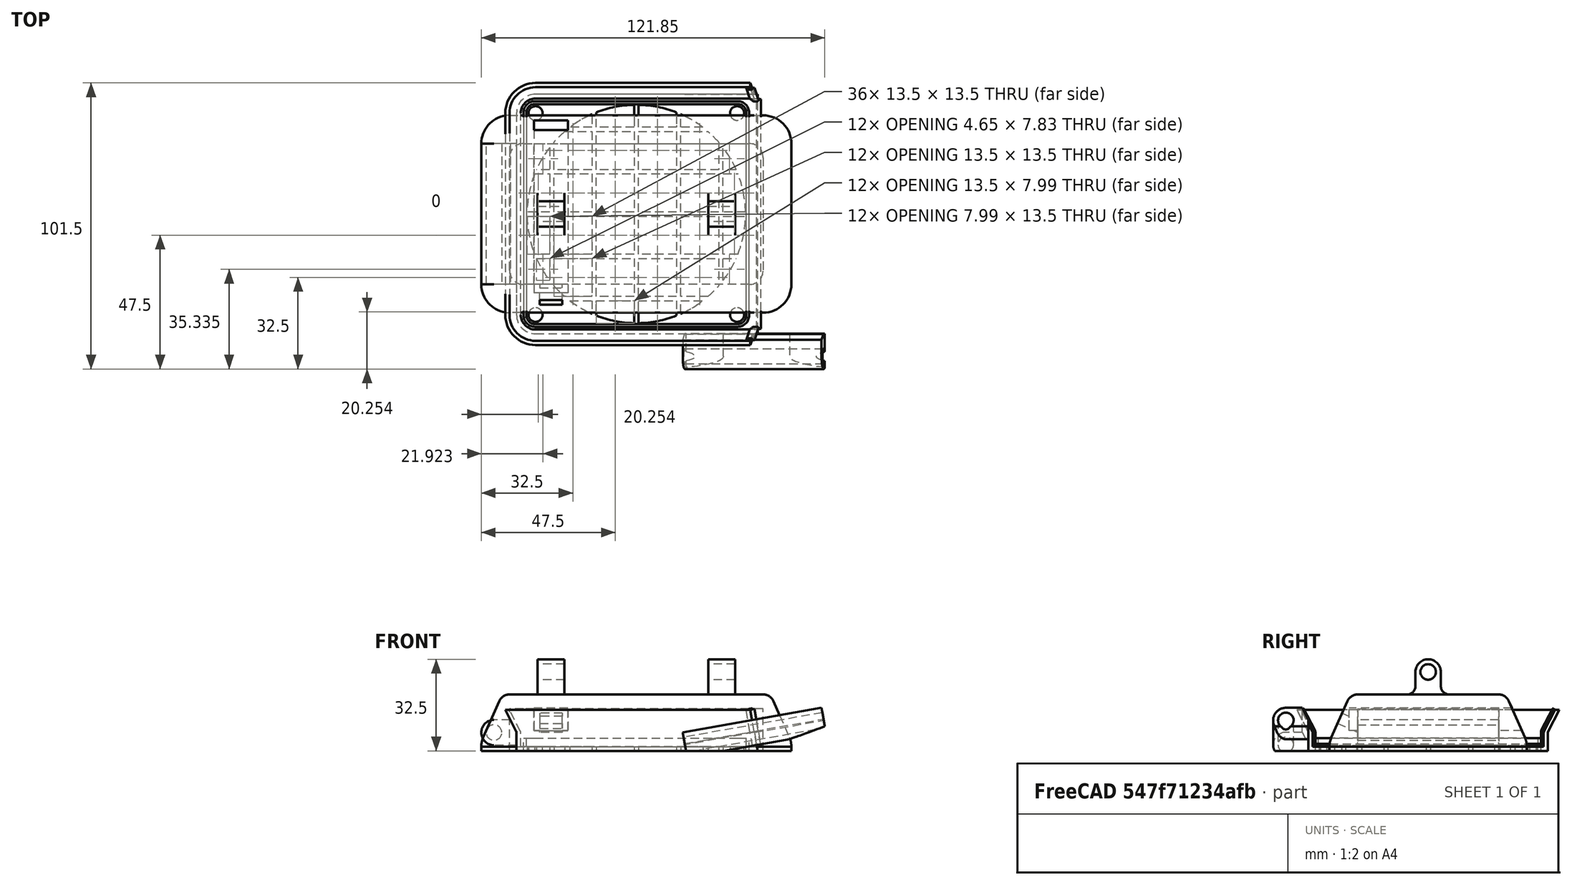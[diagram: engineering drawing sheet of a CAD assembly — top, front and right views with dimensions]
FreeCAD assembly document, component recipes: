
FREECAD ASSEMBLY — COMPONENT RECIPES ("Solder Fume Extractor 2x80mm fans")

This assembly document has 5 components, labeled P0..P4 below (a component is one placed body or linked part). 5 of them carry a construction recipe — the FreeCAD feature program that regenerates the part from scratch, quoted from this document or its linked companion documents; the rest are supplied as boundary geometry only. No exploded tour is included for this assembly.
COMPONENT P0 — recipe-attached ("Fan1Holder", modeled in this document).
Construction recipe (the document's own serialized feature program — sketch geometry with constraints, then the solid features built on it; lengths are millimeters unless a unit is written):

FEATURE [Sketcher::SketchObject] Sketch
  ArcFitTolerance = 1e-06
  AttachmentSupport = -> [XY_Plane]
  FullyConstrained = true
  MakeInternals = false
  MapMode = 5
  sketch-geometry (13):
    g0: LineSegment StartX=-42.5 StartY=35.75 StartZ=0 EndX=-42.5 EndY=-35.75 EndZ=0
    g1: LineSegment StartX=-35.75 StartY=-42.5 StartZ=0 EndX=60 EndY=-42.5 EndZ=0
    g2: LineSegment StartX=60 StartY=-42.5 StartZ=0 EndX=60 EndY=42.5 EndZ=0
    g3: LineSegment StartX=60 StartY=42.5 StartZ=0 EndX=-35.75 EndY=42.5 EndZ=0
    g4: Circle CenterX=-35.75 CenterY=35.75 CenterZ=0 NormalX=0 NormalY=0 NormalZ=1 AngleXU=0 Radius=2.5
    g5: Circle CenterX=35.75 CenterY=35.75 CenterZ=0 NormalX=0 NormalY=0 NormalZ=1 AngleXU=0 Radius=2.5
    g6: Circle CenterX=-35.75 CenterY=-35.75 CenterZ=0 NormalX=0 NormalY=0 NormalZ=1 AngleXU=0 Radius=2.5
    g7: Circle CenterX=35.75 CenterY=-35.75 CenterZ=0 NormalX=0 NormalY=0 NormalZ=1 AngleXU=0 Radius=2.5
    g8: Circle CenterX=0 CenterY=0 CenterZ=0 NormalX=0 NormalY=0 NormalZ=1 AngleXU=0 Radius=38.75
    g9: ArcOfCircle CenterX=-35.75 CenterY=35.75 CenterZ=0 NormalX=0 NormalY=0 NormalZ=1 AngleXU=0 Radius=6.75 StartAngle=1.5708 EndAngle=3.14159
    g10: GeomPoint [constr] X=-42.5 Y=42.5 Z=0
    g11: ArcOfCircle CenterX=-35.75 CenterY=-35.75 CenterZ=0 NormalX=0 NormalY=0 NormalZ=1 AngleXU=0 Radius=6.75 StartAngle=3.14159 EndAngle=4.71239
    g12: GeomPoint [constr] X=-42.5 Y=-42.5 Z=0
  constraints (30):
    c: Coincident(g1,g2)
    c: Coincident(g2,g3)
    c: Vertical(g2)
    c: Horizontal(g1)
    c: Horizontal(g3)
    c: DistanceY(g12,g10) = 85
    c: Equal(g7,g5)
    c: Equal(g5,g4)
    c: Equal(g4,g6)
    c: Diameter(g7) = 5
    c: Symmetric(g7,g5,g-1)
    c: Symmetric(g5,g4,g-2)
    c: Vertical(g6,g4)
    c: Horizontal(g6,g7)
    c: DistanceX(g4,g5) = 71.5
    c: DistanceY(g6,g4) = 71.5
    c: Symmetric(g12,g10,g-1)
    c: Coincident(g8,g-1)
    c: Diameter(g8) = 77.5
    c: DistanceX(g10,g-1) = 42.5
    c: DistanceX(g1) = 60
    c: PointOnObject(g10,g0)
    c: PointOnObject(g10,g3)
    c: Tangent(g0,g9) = -1.5708
    c: Tangent(g3,g9) = -1.5708
    c: PointOnObject(g12,g1)
    c: Tangent(g0,g11) = -1.5708
    c: Tangent(g1,g11) = -1.5708
    c: Equal(g11,g9)
    c: Coincident(g9,g4)
FEATURE [PartDesign::Pad] Pad
  Direction = (0,0,1)
  Length = 1.5
  Length2 = 10
  Profile = -> Sketch
  ReferenceAxis = -> Sketch [N_Axis]
  Refine = true
  Suppressed = false
  Type = 0
FEATURE [Sketcher::SketchObject] Sketch001
  ArcFitTolerance = 1e-06
  AttachmentSupport = -> [Pad]
  ExternalGeometry = -> [Pad]
  FullyConstrained = true
  MakeInternals = false
  MapMode = 5
  Placement = pos=(0,0,1.5) rot=(0,0,1;0rad)
  sketch-geometry (12):
    g0: LineSegment StartX=60 StartY=42.5 StartZ=0 EndX=-35.75 EndY=42.5 EndZ=0
    g1: LineSegment StartX=-42.5 StartY=35.75 StartZ=0 EndX=-42.5 EndY=-35.75 EndZ=0
    g2: LineSegment StartX=-35.75 StartY=-42.5 StartZ=0 EndX=60 EndY=-42.5 EndZ=0
    g3: ArcOfCircle CenterX=-35.75 CenterY=-35.75 CenterZ=0 NormalX=0 NormalY=0 NormalZ=1 AngleXU=0 Radius=6.75 StartAngle=3.14159 EndAngle=4.71239
    g4: ArcOfCircle CenterX=-35.75 CenterY=35.75 CenterZ=0 NormalX=0 NormalY=0 NormalZ=1 AngleXU=0 Radius=6.75 StartAngle=1.5708 EndAngle=3.14159
    g5: LineSegment StartX=60 StartY=-42.5 StartZ=0 EndX=60 EndY=-41 EndZ=0
    g6: LineSegment StartX=60 StartY=-41 StartZ=0 EndX=-35.75 EndY=-41 EndZ=0
    g7: LineSegment StartX=-41 StartY=-35.75 StartZ=0 EndX=-41 EndY=35.75 EndZ=0
    g8: LineSegment StartX=-35.75 StartY=41 StartZ=0 EndX=60 EndY=41 EndZ=0
    g9: LineSegment StartX=60 StartY=41 StartZ=0 EndX=60 EndY=42.5 EndZ=0
    g10: ArcOfCircle CenterX=-35.75 CenterY=-35.75 CenterZ=0 NormalX=0 NormalY=0 NormalZ=1 AngleXU=0 Radius=5.25 StartAngle=3.14159 EndAngle=4.71239
    g11: ArcOfCircle CenterX=-35.75 CenterY=35.75 CenterZ=0 NormalX=0 NormalY=0 NormalZ=1 AngleXU=0 Radius=5.25 StartAngle=1.5708 EndAngle=3.14159
  constraints (30):
    c: Coincident(g0,g-3)
    c: Coincident(g0,g-4)
    c: Horizontal(g2)
    c: Symmetric(g2,g0,g-1)
    c: Equal(g2,g0)
    c: Coincident(g-5,g1)
    c: Coincident(g1,g-5)
    c: Coincident(g3,g2)
    c: Coincident(g3,g1)
    c: Coincident(g4,g1)
    c: Coincident(g4,g0)
    c: Equal(g4,g-4)
    c: Equal(g-4,g3)
    c: Coincident(g5,g2)
    c: Vertical(g5)
    c: Coincident(g6,g5)
    c: Horizontal(g6)
    c: Vertical(g7)
    c: Coincident(g9,g8)
    c: Coincident(g9,g0)
    c: Horizontal(g8)
    c: Vertical(g9)
    c: Equal(g5,g9)
    c: Equal(g6,g8)
    c: Tangent(g10,g6) = 1.5708
    c: Tangent(g10,g7) = 1.5708
    c: Tangent(g11,g7) = 1.5708
    c: Tangent(g11,g8) = 1.5708
    c: DistanceY(g5,g5) = 1.5
    c: Coincident(g11,g4)
FEATURE [PartDesign::Pad] Pad001
  BaseFeature = -> Pad
  Direction = (0,0,1)
  Length = 5
  Length2 = 10
  Profile = -> Sketch001
  ReferenceAxis = -> Sketch001 [N_Axis]
  Refine = true
  Suppressed = false
  Type = 0
FEATURE [Sketcher::SketchObject] Sketch002
  ArcFitTolerance = 1e-06
  AttachmentSupport = -> [Pad001]
  ExternalGeometry = -> [Pad001]
  FullyConstrained = true
  MakeInternals = false
  MapMode = 5
  Placement = pos=(60,0,0) rot=(0.57735,0.57735,0.57735;2.0944rad)
  sketch-geometry (6):
    g0: LineSegment StartX=41.1112 StartY=6.9583 StartZ=0 EndX=45 EndY=14.5 EndZ=0
    g1: LineSegment StartX=45 StartY=14.5 StartZ=0 EndX=46.5 EndY=14.5 EndZ=0
    g2: LineSegment StartX=46.5 StartY=14.5 StartZ=0 EndX=42.6112 EndY=6.9583 EndZ=0
    g3: ArcOfCircle CenterX=43.5 CenterY=6.5 CenterZ=0 NormalX=0 NormalY=0 NormalZ=1 AngleXU=0 Radius=1 StartAngle=2.66551 EndAngle=3.14159
    g4: ArcOfCircle CenterX=42 CenterY=6.5 CenterZ=0 NormalX=0 NormalY=0 NormalZ=1 AngleXU=0 Radius=1 StartAngle=2.66551 EndAngle=3.14159
    g5: LineSegment StartX=42.5 StartY=6.5 StartZ=0 EndX=41 EndY=6.5 EndZ=0
  constraints (16):
    c: Coincident(g0,g1)
    c: Horizontal(g1)
    c: Coincident(g1,g2)
    c: Coincident(g3,g-3)
    c: Coincident(g4,g-3)
    c: Tangent(g4,g0) = 1.5708
    c: Tangent(g3,g2) = -1.5708
    c: Coincident(g5,g3)
    c: Coincident(g5,g4)
    c: Perpendicular(g3,g5)
    c: Perpendicular(g4,g5)
    c: Equal(g1,g5)
    c: Radius(g4) = 1
    c: DistanceY(g3,g1) = 8
    c: DistanceX(g3,g1) = 4
    c: Equal(g4,g3)
FEATURE [PartDesign::AdditivePipe] AdditivePipe
  AuxilleryCurvelinear = true
  AuxillerySpineTangent = false
  BaseFeature = -> Pad001
  Binormal = (0,0,0)
  Mode = 0
  Profile = -> Sketch002
  Refine = true
  Spine = -> Pad001 [Edge32,Edge33,Edge34,Edge35,Edge36]
  SpineTangent = false
  Suppressed = false
  Transformation = 0
  Transition = 0
FEATURE [Sketcher::SketchObject] Sketch003
  ArcFitTolerance = 1e-06
  AttachmentSupport = -> [XY_Plane]
  ExternalGeometry = -> [AdditivePipe]
  FullyConstrained = true
  MakeInternals = false
  MapMode = 5
  sketch-geometry (5):
    g0: LineSegment StartX=-30.75 StartY=42.5 StartZ=0 EndX=-30.75 EndY=-42.5 EndZ=0
    g1: LineSegment StartX=-30.75 StartY=-42.5 StartZ=0 EndX=-29.25 EndY=-42.5 EndZ=0
    g2: LineSegment StartX=-29.25 StartY=-42.5 StartZ=0 EndX=-29.25 EndY=42.5 EndZ=0
    g3: LineSegment StartX=-29.25 StartY=42.5 StartZ=0 EndX=-30.75 EndY=42.5 EndZ=0
    g4: GeomPoint [constr] X=-30 Y=0 Z=0
  constraints (13):
    c: Coincident(g0,g1)
    c: Coincident(g1,g2)
    c: Coincident(g2,g3)
    c: Coincident(g3,g0)
    c: Vertical(g0)
    c: Vertical(g2)
    c: Horizontal(g1)
    c: Horizontal(g3)
    c: Symmetric(g2,g0,g4)
    c: PointOnObject(g4,g-1)
    c: PointOnObject(g1,g-3)
    c: DistanceX(g3,g3) = 1.5
    c: DistanceX(g4,g-1) = 30
FEATURE [PartDesign::Pad] Pad002
  BaseFeature = -> AdditivePipe
  Direction = (0,0,1)
  Length = 10
  Length2 = 10
  Profile = -> Sketch003
  ReferenceAxis = -> Sketch003 [N_Axis]
  Refine = true
  Suppressed = false
  Type = 3
  UpToFace = -> AdditivePipe [Face2]
FEATURE [PartDesign::LinearPattern] LinearPattern
  BaseFeature = -> Pad002
  Direction = -> Sketch003 [H_Axis]
  Length = 60
  Mode = 0
  Occurrences = 5
  Offset = 15
  Originals = -> [Pad002]
  Refine = true
  Suppressed = false
  TransformMode = 0
FEATURE [Sketcher::SketchObject] Sketch004
  ArcFitTolerance = 1e-06
  AttachmentSupport = -> [XY_Plane]
  ExternalGeometry = -> [LinearPattern]
  FullyConstrained = true
  MakeInternals = false
  MapMode = 5
  sketch-geometry (5):
    g0: LineSegment StartX=42.5 StartY=29.25 StartZ=0 EndX=42.5 EndY=30.75 EndZ=0
    g1: LineSegment StartX=42.5 StartY=30.75 StartZ=0 EndX=-42.5 EndY=30.75 EndZ=0
    g2: LineSegment StartX=-42.5 StartY=30.75 StartZ=0 EndX=-42.5 EndY=29.25 EndZ=0
    g3: LineSegment StartX=-42.5 StartY=29.25 StartZ=0 EndX=42.5 EndY=29.25 EndZ=0
    g4: GeomPoint [constr] X=0 Y=30 Z=0
  constraints (13):
    c: Coincident(g0,g1)
    c: Coincident(g1,g2)
    c: Coincident(g2,g3)
    c: Coincident(g3,g0)
    c: Vertical(g0)
    c: Vertical(g2)
    c: Horizontal(g1)
    c: Horizontal(g3)
    c: Symmetric(g2,g0,g4)
    c: PointOnObject(g4,g-2)
    c: PointOnObject(g1,g-3)
    c: DistanceY(g4) = 30
    c: DistanceY(g0,g0) = 1.5
FEATURE [PartDesign::Pad] Pad003
  BaseFeature = -> LinearPattern
  Direction = (0,0,1)
  Length = 10
  Length2 = 10
  Profile = -> Sketch004
  ReferenceAxis = -> Sketch004 [N_Axis]
  Refine = true
  Suppressed = false
  Type = 3
  UpToFace = -> LinearPattern [Face31]
FEATURE [PartDesign::LinearPattern] LinearPattern001
  BaseFeature = -> Pad003
  Direction = -> Sketch004 [V_Axis]
  Length = 60
  Mode = 0
  Occurrences = 5
  Offset = 15
  Originals = -> [Pad003]
  Refine = true
  Reversed = true
  Suppressed = false
  TransformMode = 0
FEATURE [PartDesign::CoordinateSystem] FanMountHole
  AttacherType = Attacher::AttachEngine3D
  AttachmentSupport = -> [LinearPattern001]
  MapMode = 11
  Placement = pos=(-35.75,-35.75,0) rot=(0,0,1;1.5708rad)
FEATURE [Sketcher::SketchObject] Sketch005
  ArcFitTolerance = 1e-06
  AttachmentSupport = -> [XZ_Plane]
  ExternalGeometry = -> [LinearPattern001]
  FullyConstrained = true
  MakeInternals = false
  MapMode = 5
  Placement = pos=(0,0,0) rot=(1,0,0;1.5708rad)
  sketch-geometry (4):
    g0: LineSegment StartX=60 StartY=14.5 StartZ=0 EndX=60 EndY=0 EndZ=0
    g1: LineSegment StartX=60 StartY=0 StartZ=0 EndX=43 EndY=0 EndZ=0
    g2: LineSegment StartX=43 StartY=0 StartZ=0 EndX=40.4433 EndY=14.5 EndZ=0
    g3: LineSegment StartX=40.4433 StartY=14.5 StartZ=0 EndX=60 EndY=14.5 EndZ=0
  constraints (11):
    c: Coincident(g-3,g0)
    c: PointOnObject(g0,g-1)
    c: Vertical(g0)
    c: Coincident(g0,g1)
    c: PointOnObject(g1,g-1)
    c: Coincident(g1,g2)
    c: PointOnObject(g2,g-3)
    c: Coincident(g2,g3)
    c: Coincident(g3,g0)
    c: DistanceX(g-1,g1) = 43
    c: Angle(g1,g2) = 1.74533
FEATURE [PartDesign::Pocket] Pocket
  BaseFeature = -> LinearPattern001
  Direction = (0,1,-2e-16)
  Length = 5
  Length2 = 5
  Midplane = true
  Profile = -> Sketch005
  ReferenceAxis = -> Sketch005 [N_Axis]
  Refine = true
  Suppressed = false
  Type = 1
FEATURE [PartDesign::CoordinateSystem] OtherFanHolder
  AttacherType = Attacher::AttachEngine3D
  AttachmentSupport = -> [Pocket]
  MapMode = 45
  Placement = pos=(42.8701,0,0.736527) rot=(0.642788,0,0.766044;3.14159rad)
FEATURE [PartDesign::CoordinateSystem] FilterHolderMount
  AttacherType = Attacher::AttachEngine3D
  AttachmentSupport = -> [Pocket]
  MapMode = 11
  Placement = pos=(-35.75,35.75,1.5) rot=(0,0,1;1.5708rad)
FEATURE [Sketcher::SketchObject] Sketch010
  ArcFitTolerance = 1e-06
  AttachmentSupport = -> [XZ_Plane]
  ExternalGeometry = -> [Pocket]
  FullyConstrained = true
  MakeInternals = false
  MapMode = 5
  Placement = pos=(0,0,0) rot=(1,0,0;1.5708rad)
  sketch-geometry (7):
    g0: ArcOfCircle CenterX=-43.5 CenterY=6.5 CenterZ=0 NormalX=0 NormalY=0 NormalZ=1 AngleXU=0 Radius=1 StartAngle=-2.4e-14 EndAngle=0.476081
    g1: LineSegment StartX=-42.5 StartY=6.5 StartZ=0 EndX=-42.5 EndY=2 EndZ=0
    g2: LineSegment StartX=-42.5 StartY=2 StartZ=0 EndX=-50.5 EndY=2 EndZ=0
    g3: LineSegment StartX=-42.6112 StartY=6.9583 StartZ=0 EndX=-44.6953 EndY=11 EndZ=0
    g4: LineSegment StartX=-44.6953 StartY=11 StartZ=0 EndX=-50.5 EndY=11 EndZ=0
    g5: ArcOfCircle CenterX=-50.5 CenterY=6.5 CenterZ=0 NormalX=0 NormalY=0 NormalZ=1 AngleXU=0 Radius=4.5 StartAngle=1.5708 EndAngle=4.71239
    g6: Circle CenterX=-50.5 CenterY=6.5 CenterZ=0 NormalX=0 NormalY=0 NormalZ=1 AngleXU=0 Radius=2.75
  constraints (18):
    c: Coincident(g0,g-5)
    c: Coincident(g0,g-5)
    c: Equal(g-5,g0)
    c: Coincident(g1,g0)
    c: PointOnObject(g1,g-3)
    c: Coincident(g2,g1)
    c: Horizontal(g2)
    c: Coincident(g3,g0)
    c: PointOnObject(g3,g-4)
    c: Horizontal(g4)
    c: Tangent(g5,g4) = -1.5708
    c: Tangent(g5,g2) = 1.5708
    c: Diameter(g5) = 9
    c: Diameter(g6) = 5.5
    c: Coincident(g6,g5)
    c: Horizontal(g0,g5)
    c: Coincident(g3,g4)
    c: DistanceX(g5,g-4) = 4
FEATURE [PartDesign::Pad] Pad008
  BaseFeature = -> Pocket
  Direction = (0,-1,2e-16)
  Length = 50
  Length2 = 10
  Midplane = true
  Profile = -> Sketch010
  ReferenceAxis = -> Sketch010 [N_Axis]
  Refine = true
  Suppressed = false
  Type = 0
FEATURE [Sketcher::SketchObject] Sketch011
  ArcFitTolerance = 1e-06
  AttachmentSupport = -> [Pad008]
  ExternalGeometry = -> [Pad008]
  FullyConstrained = true
  MakeInternals = false
  MapMode = 5
  Placement = pos=(41.7034,1.6e-15,7.35343) rot=(0.540716,0.540716,0.6444;1.99673rad)
  sketch-geometry (7):
    g0: ArcOfCircle CenterX=-43.0908 CenterY=-0.761797 CenterZ=0 NormalX=0 NormalY=0 NormalZ=1 AngleXU=0 Radius=0.6 StartAngle=6.10761 EndAngle=6.92787
    g1: LineSegment StartX=-44.66 StartY=3.6334 StartZ=0 EndX=-42.6112 EndY=-0.401229 EndZ=0
    g2: LineSegment StartX=-42.5 StartY=-5.3666 StartZ=0 EndX=-42.5 EndY=-0.866599 EndZ=0
    g3: LineSegment StartX=-42.5 StartY=-5.3666 StartZ=0 EndX=-50.5 EndY=-5.3666 EndZ=0
    g4: LineSegment StartX=-44.66 StartY=3.6334 StartZ=0 EndX=-50.5 EndY=3.6334 EndZ=0
    g5: ArcOfCircle CenterX=-50.5 CenterY=-0.866599 CenterZ=0 NormalX=0 NormalY=0 NormalZ=1 AngleXU=0 Radius=4.5 StartAngle=1.5708 EndAngle=4.71239
    g6: Circle CenterX=-50.5 CenterY=-0.866599 CenterZ=0 NormalX=0 NormalY=0 NormalZ=1 AngleXU=0 Radius=2.75
  constraints (18):
    c: Coincident(g0,g-3)
    c: Coincident(g0,g-4)
    c: Radius(g0) = 0.6
    c: Coincident(g3,g2)
    c: Horizontal(g3)
    c: Coincident(g4,g1)
    c: Horizontal(g4)
    c: Tangent(g5,g4) = -1.5708
    c: Tangent(g5,g3) = 1.5708
    c: Diameter(g5) = 9
    c: Horizontal(g5,g2)
    c: Coincident(g6,g5)
    c: Diameter(g6) = 5.5
    c: DistanceX(g5,g-4) = 4
    c: Coincident(g2,g0)
    c: PointOnObject(g1,g-4)
    c: PointOnObject(g2,g-3)
    c: Coincident(g0,g1)
FEATURE [PartDesign::Pad] Pad009
  BaseFeature = -> Pad008
  Direction = (0.984808,-2e-16,0.173648)
  Length = 50
  Length2 = 10
  Midplane = true
  Profile = -> Sketch011
  ReferenceAxis = -> Sketch011 [N_Axis]
  Refine = true
  Suppressed = false
  Type = 0
FEATURE [Sketcher::SketchObject] Sketch031
  ArcFitTolerance = 1e-06
  AttachmentSupport = -> [XZ_Plane]
  FullyConstrained = true
  MakeInternals = false
  MapMode = 5
  Placement = pos=(0,0,0) rot=(1,0,0;1.5708rad)
  sketch-geometry (8):
    g0: LineSegment StartX=0 StartY=0 StartZ=0 EndX=0 EndY=-5 EndZ=0
    g1: LineSegment StartX=0 StartY=-5 StartZ=0 EndX=43 EndY=-5 EndZ=0
    g2: LineSegment StartX=43 StartY=-5 StartZ=0 EndX=43 EndY=1.24e-14 EndZ=0
    g3: LineSegment StartX=43 StartY=1.24e-14 StartZ=0 EndX=0 EndY=0 EndZ=0
    g4: LineSegment StartX=43 StartY=1.24e-14 StartZ=0 EndX=44.7101 EndY=-4.69846 EndZ=0
    g5: LineSegment StartX=44.7101 StartY=-4.69846 StartZ=0 EndX=85.1169 EndY=10.0084 EndZ=0
    g6: LineSegment StartX=85.1169 StartY=10.0084 StartZ=0 EndX=83.4068 EndY=14.7069 EndZ=0
    g7: LineSegment StartX=83.4068 StartY=14.7069 StartZ=0 EndX=43 EndY=1.24e-14 EndZ=0
  constraints (22):
    c: Angle(g-3,g-1) = 1.39626
    c: Coincident(g0,g1)
    c: Coincident(g1,g2)
    c: Coincident(g2,g3)
    c: Coincident(g3,g0)
    c: Vertical(g0)
    c: Vertical(g2)
    c: Horizontal(g1)
    c: Coincident(g0,g-1)
    c: Coincident(g2,g-3)
    c: DistanceY(g2,g2) = 5
    c: Coincident(g2,g4)
    c: Coincident(g4,g5)
    c: Coincident(g5,g6)
    c: Coincident(g6,g7)
    c: Coincident(g7,g4)
    c: Perpendicular(g7,g4)
    c: Perpendicular(g6,g7)
    c: Equal(g4,g6)
    c: Equal(g6,g2)
    c: Equal(g7,g1)
    c: Angle(g7,g-3) = 1.39626
FEATURE [PartDesign::Pocket] Pocket008
  BaseFeature = -> Pad009
  Direction = (0,1,-2e-16)
  Length = 5
  Length2 = 5
  Profile = -> Sketch031
  ReferenceAxis = -> Sketch031 [N_Axis]
  Refine = true
  Reversed = true
  Suppressed = false
  Type = 1
FEATURE [PartDesign::CoordinateSystem] Mount1
  AttacherType = Attacher::AttachEngine3D
  AttachmentSupport = -> [Pocket008]
  MapMode = 45
  Placement = pos=(-50.5,-7e-16,6.5) rot=(0,0.707107,0.707107;3.14159rad)
FEATURE [PartDesign::CoordinateSystem] Mount2
  AttacherType = Attacher::AttachEngine3D
  AttachmentOffset = pos=(0,0,25) rot=(0,0,1;0rad)
  AttachmentSupport = -> [Pocket008]
  MapMode = 11
  Placement = pos=(41.8539,-50.5,6.5) rot=(0.642788,0,0.766044;3.14159rad)
FEATURE [Sketcher::SketchObject] Sketch032
  ArcFitTolerance = 1e-06
  AttachmentSupport = -> [XZ_Plane]
  ExternalGeometry = -> [Pocket008]
  FullyConstrained = true
  MakeInternals = false
  MapMode = 5
  Placement = pos=(0,0,0) rot=(1,0,0;1.5708rad)
  sketch-geometry (7):
    g0: LineSegment StartX=41.2355 StartY=1.5 StartZ=0 EndX=42.7355 EndY=1.5 EndZ=0
    g1: LineSegment StartX=42.7355 StartY=1.5 StartZ=0 EndX=44.145 EndY=2.01303 EndZ=0
    g2: ArcOfCircle CenterX=41.2355 CenterY=2.10733 CenterZ=0 NormalX=0 NormalY=0 NormalZ=1 AngleXU=0 Radius=0.607328 StartAngle=4.71239 EndAngle=6.06406
    g3: ArcOfCircle CenterX=43.9373 CenterY=2.58373 CenterZ=0 NormalX=0 NormalY=0 NormalZ=1 AngleXU=0 Radius=0.607328 StartAngle=3.70978 EndAngle=5.06145
    g4: LineSegment StartX=42.3157 StartY=2.4414 StartZ=0 EndX=42.8081 EndY=2.52822 EndZ=0
    g5: ArcOfCircle CenterX=42.4211 CenterY=1.84329 CenterZ=0 NormalX=0 NormalY=0 NormalZ=1 AngleXU=0 Radius=0.607328 StartAngle=1.74533 EndAngle=2.92247
    g6: ArcOfCircle CenterX=42.9135 CenterY=1.93012 CenterZ=0 NormalX=0 NormalY=0 NormalZ=1 AngleXU=0 Radius=0.607328 StartAngle=0.568188 EndAngle=1.74533
  constraints (17):
    c: Coincident(g0,g-4)
    c: Horizontal(g0)
    c: Coincident(g0,g1)
    c: DistanceX(g0,g0) = 1.5
    c: Angle(g1,g-4) = 1.39626
    c: Symmetric(g4,g4,g-4)
    c: Tangent(g5,g4) = 1.5708
    c: Tangent(g5,g2) = 1.5708
    c: Tangent(g6,g4) = 1.5708
    c: Tangent(g6,g3) = 1.5708
    c: Tangent(g3,g1) = -1.5708
    c: Tangent(g2,g0) = -1.5708
    c: Equal(g2,g5)
    c: Equal(g5,g6)
    c: Equal(g6,g3)
    c: Distance(g0,g4) = 1
    c: Distance(g4) = 0.5
FEATURE [PartDesign::AdditivePipe] AdditivePipe002
  AuxilleryCurvelinear = true
  AuxillerySpineTangent = false
  BaseFeature = -> Pocket008
  Binormal = (0,0,0)
  Mode = 0
  Profile = -> Sketch032
  Refine = true
  Spine = -> Pocket008 [Edge9,Edge146,Edge145,Edge144,Edge2,Edge147,Edge148]
  SpineTangent = false
  Suppressed = false
  Transformation = 0
  Transition = 1
FEATURE [PartDesign::Body] Body  label="Fan1Holder"
  AllowCompound = false
  Group = -> [Sketch,Pad,Sketch001,Pad001,Sketch002,AdditivePipe,Sketch003,Pad002,LinearPattern,Sketch004,Pad003,LinearPattern001,FanMountHole,Sketch005,Pocket,OtherFanHolder,FilterHolderMount,Sketch010,Pad008,Sketch011,Pad009,Mount1,Mount2,Sketch031,Pocket008,Sketch032,AdditivePipe002]
  Origin = -> Origin
  Tip = -> AdditivePipe002
COMPONENT P1 — recipe-attached ("FilterHolder", modeled in this document).
Construction recipe (the document's own serialized feature program — sketch geometry with constraints, then the solid features built on it; lengths are millimeters unless a unit is written):

FEATURE [Sketcher::SketchObject] Sketch006
  ArcFitTolerance = 1e-06
  AttachmentSupport = -> [XY_Plane002]
  FullyConstrained = true
  MakeInternals = false
  MapMode = 5
  sketch-geometry (15):
    g0: LineSegment StartX=40 StartY=-36 StartZ=0 EndX=40 EndY=36 EndZ=0
    g1: LineSegment StartX=36 StartY=40 StartZ=0 EndX=-36 EndY=40 EndZ=0
    g2: LineSegment StartX=-40 StartY=36 StartZ=0 EndX=-40 EndY=-36 EndZ=0
    g3: LineSegment StartX=-36 StartY=-40 StartZ=0 EndX=36 EndY=-40 EndZ=0
    g4: ArcOfCircle CenterX=36 CenterY=-36 CenterZ=0 NormalX=0 NormalY=0 NormalZ=1 AngleXU=0 Radius=4 StartAngle=4.71239 EndAngle=6.28319
    g5: ArcOfCircle CenterX=36 CenterY=36 CenterZ=0 NormalX=0 NormalY=0 NormalZ=1 AngleXU=0 Radius=4 StartAngle=2e-16 EndAngle=1.5708
    g6: ArcOfCircle CenterX=-36 CenterY=36 CenterZ=0 NormalX=0 NormalY=0 NormalZ=1 AngleXU=0 Radius=4 StartAngle=1.5708 EndAngle=3.14159
    g7: ArcOfCircle CenterX=-36 CenterY=-36 CenterZ=0 NormalX=0 NormalY=0 NormalZ=1 AngleXU=0 Radius=4 StartAngle=3.14159 EndAngle=4.71239
    g8: GeomPoint [constr] X=40 Y=-40 Z=0
    g9: GeomPoint [constr] X=-40 Y=40 Z=0
    g10: Circle CenterX=-35.75 CenterY=35.75 CenterZ=0 NormalX=0 NormalY=0 NormalZ=1 AngleXU=0 Radius=2.5
    g11: Circle CenterX=35.75 CenterY=35.75 CenterZ=0 NormalX=0 NormalY=0 NormalZ=1 AngleXU=0 Radius=2.5
    g12: Circle CenterX=35.75 CenterY=-35.75 CenterZ=0 NormalX=0 NormalY=0 NormalZ=1 AngleXU=0 Radius=2.5
    g13: Circle CenterX=-35.75 CenterY=-35.75 CenterZ=0 NormalX=0 NormalY=0 NormalZ=1 AngleXU=0 Radius=2.5
    g14: Circle CenterX=0 CenterY=0 CenterZ=0 NormalX=0 NormalY=0 NormalZ=1 AngleXU=0 Radius=38.75
  constraints (34):
    c: Tangent(g0,g4) = -1.5708
    c: Tangent(g0,g5) = -1.5708
    c: Tangent(g1,g5) = -1.5708
    c: Tangent(g1,g6) = -1.5708
    c: Tangent(g2,g6) = -1.5708
    c: Tangent(g2,g7) = -1.5708
    c: Tangent(g3,g7) = -1.5708
    c: Tangent(g3,g4) = -1.5708
    c: Vertical(g2)
    c: Horizontal(g1)
    c: Equal(g4,g5)
    c: Equal(g5,g6)
    c: Equal(g6,g7)
    c: PointOnObject(g8,g0)
    c: PointOnObject(g8,g3)
    c: PointOnObject(g9,g1)
    c: PointOnObject(g9,g2)
    c: Radius(g7) = 4
    c: Symmetric(g3,g3,g-2)
    c: Symmetric(g0,g0,g-1)
    c: Equal(g0,g3)
    c: DistanceY(g3,g1) = 80
    c: Equal(g10,g11)
    c: Equal(g11,g12)
    c: Equal(g12,g13)
    c: Symmetric(g10,g11,g-2)
    c: Symmetric(g11,g12,g-1)
    c: Horizontal(g12,g13)
    c: Vertical(g13,g10)
    c: DistanceY(g13,g10) = 71.5
    c: DistanceX(g10,g11) = 71.5
    c: Diameter(g11) = 5
    c: Coincident(g14,g-1)
    c: Diameter(g14) = 77.5
FEATURE [PartDesign::Pad] Pad004
  Direction = (0,0,1)
  Length = 1.5
  Length2 = 10
  Profile = -> Sketch006
  ReferenceAxis = -> Sketch006 [N_Axis]
  Refine = true
  Suppressed = false
  Type = 0
FEATURE [Sketcher::SketchObject] Sketch007
  ArcFitTolerance = 1e-06
  AttachmentSupport = -> [XY_Plane002]
  ExternalGeometry = -> [Pad004]
  FullyConstrained = true
  MakeInternals = false
  MapMode = 5
  sketch-geometry (5):
    g0: LineSegment StartX=-29.25 StartY=-40 StartZ=0 EndX=-29.25 EndY=40 EndZ=0
    g1: LineSegment StartX=-29.25 StartY=40 StartZ=0 EndX=-30.75 EndY=40 EndZ=0
    g2: LineSegment StartX=-30.75 StartY=40 StartZ=0 EndX=-30.75 EndY=-40 EndZ=0
    g3: LineSegment StartX=-30.75 StartY=-40 StartZ=0 EndX=-29.25 EndY=-40 EndZ=0
    g4: GeomPoint [constr] X=-30 Y=0 Z=0
  constraints (13):
    c: Coincident(g0,g1)
    c: Coincident(g1,g2)
    c: Coincident(g2,g3)
    c: Coincident(g3,g0)
    c: Vertical(g0)
    c: Vertical(g2)
    c: Horizontal(g1)
    c: Horizontal(g3)
    c: Symmetric(g2,g0,g4)
    c: PointOnObject(g4,g-1)
    c: PointOnObject(g1,g-3)
    c: DistanceX(g4,g-1) = 30
    c: DistanceX(g1,g1) = 1.5
FEATURE [PartDesign::Pad] Pad005
  BaseFeature = -> Pad004
  Direction = (0,0,1)
  Length = 10
  Length2 = 10
  Profile = -> Sketch007
  ReferenceAxis = -> Sketch007 [N_Axis]
  Refine = true
  Suppressed = false
  Type = 3
  UpToFace = -> Pad004 [Face15]
FEATURE [PartDesign::LinearPattern] LinearPattern002
  BaseFeature = -> Pad005
  Direction = -> Sketch007 [H_Axis]
  Length = 60
  Mode = 0
  Occurrences = 5
  Offset = 15
  Originals = -> [Pad005]
  Refine = true
  Suppressed = false
  TransformMode = 0
FEATURE [Sketcher::SketchObject] Sketch008
  ArcFitTolerance = 1e-06
  AttachmentSupport = -> [XY_Plane002]
  ExternalGeometry = -> [LinearPattern002]
  FullyConstrained = true
  MakeInternals = false
  MapMode = 5
  sketch-geometry (5):
    g0: LineSegment StartX=40 StartY=-30.75 StartZ=0 EndX=40 EndY=-29.25 EndZ=0
    g1: LineSegment StartX=40 StartY=-29.25 StartZ=0 EndX=-40 EndY=-29.25 EndZ=0
    g2: LineSegment StartX=-40 StartY=-29.25 StartZ=0 EndX=-40 EndY=-30.75 EndZ=0
    g3: LineSegment StartX=-40 StartY=-30.75 StartZ=0 EndX=40 EndY=-30.75 EndZ=0
    g4: GeomPoint [constr] X=0 Y=-30 Z=0
  constraints (13):
    c: Coincident(g0,g1)
    c: Coincident(g1,g2)
    c: Coincident(g2,g3)
    c: Coincident(g3,g0)
    c: Vertical(g0)
    c: Vertical(g2)
    c: Horizontal(g1)
    c: Horizontal(g3)
    c: Symmetric(g2,g0,g4)
    c: PointOnObject(g4,g-2)
    c: PointOnObject(g1,g-3)
    c: DistanceY(g4,g-1) = 30
    c: DistanceY(g0,g0) = 1.5
FEATURE [PartDesign::Pad] Pad006
  BaseFeature = -> LinearPattern002
  Direction = (0,0,1)
  Length = 10
  Length2 = 10
  Profile = -> Sketch008
  ReferenceAxis = -> Sketch008 [N_Axis]
  Refine = true
  Suppressed = false
  Type = 3
  UpToFace = -> LinearPattern002 [Face32]
FEATURE [PartDesign::LinearPattern] LinearPattern003
  BaseFeature = -> Pad006
  Direction = -> Sketch008 [V_Axis]
  Length = 60
  Mode = 0
  Occurrences = 5
  Offset = 15
  Originals = -> [Pad006]
  Refine = true
  Suppressed = false
  TransformMode = 0
FEATURE [Sketcher::SketchObject] Sketch009
  ArcFitTolerance = 1e-06
  AttachmentSupport = -> [LinearPattern003]
  ExternalGeometry = -> [LinearPattern003]
  FullyConstrained = true
  MakeInternals = false
  MapMode = 5
  Placement = pos=(0,0,1.5) rot=(0,0,1;0rad)
  sketch-geometry (20):
    g0: LineSegment StartX=-40 StartY=36 StartZ=0 EndX=-40 EndY=-36 EndZ=0
    g1: LineSegment StartX=-36 StartY=-40 StartZ=0 EndX=36 EndY=-40 EndZ=0
    g2: LineSegment StartX=40 StartY=-36 StartZ=0 EndX=40 EndY=36 EndZ=0
    g3: LineSegment StartX=36 StartY=40 StartZ=0 EndX=-36 EndY=40 EndZ=0
    g4: ArcOfCircle CenterX=-36 CenterY=36 CenterZ=0 NormalX=0 NormalY=0 NormalZ=1 AngleXU=0 Radius=4 StartAngle=1.5708 EndAngle=3.14159
    g5: ArcOfCircle CenterX=-36 CenterY=-36 CenterZ=0 NormalX=0 NormalY=0 NormalZ=1 AngleXU=0 Radius=4 StartAngle=3.14159 EndAngle=4.71239
    g6: ArcOfCircle CenterX=36 CenterY=-36 CenterZ=0 NormalX=0 NormalY=0 NormalZ=1 AngleXU=0 Radius=4 StartAngle=4.71239 EndAngle=6.28319
    g7: ArcOfCircle CenterX=36 CenterY=36 CenterZ=0 NormalX=0 NormalY=0 NormalZ=1 AngleXU=0 Radius=4 StartAngle=-9e-16 EndAngle=1.5708
    g8: GeomPoint [constr] X=-40 Y=40 Z=0
    g9: GeomPoint [constr] X=40 Y=-40 Z=0
    g10: LineSegment StartX=-39 StartY=36 StartZ=0 EndX=-39 EndY=-36 EndZ=0
    g11: LineSegment StartX=-36 StartY=-39 StartZ=0 EndX=36 EndY=-39 EndZ=0
    g12: LineSegment StartX=39 StartY=-36 StartZ=0 EndX=39 EndY=36 EndZ=0
    g13: LineSegment StartX=36 StartY=39 StartZ=0 EndX=-36 EndY=39 EndZ=0
    g14: ArcOfCircle CenterX=-36 CenterY=36 CenterZ=0 NormalX=0 NormalY=0 NormalZ=1 AngleXU=0 Radius=3 StartAngle=1.5708 EndAngle=3.14159
    g15: ArcOfCircle CenterX=-36 CenterY=-36 CenterZ=0 NormalX=0 NormalY=0 NormalZ=1 AngleXU=0 Radius=3 StartAngle=3.14159 EndAngle=4.71239
    g16: ArcOfCircle CenterX=36 CenterY=-36 CenterZ=0 NormalX=0 NormalY=0 NormalZ=1 AngleXU=0 Radius=3 StartAngle=4.71239 EndAngle=6.28319
    g17: ArcOfCircle CenterX=36 CenterY=36 CenterZ=0 NormalX=0 NormalY=0 NormalZ=1 AngleXU=0 Radius=3 StartAngle=-9e-16 EndAngle=1.5708
    g18: GeomPoint [constr] X=-39 Y=39 Z=0
    g19: GeomPoint [constr] X=39 Y=-39 Z=0
  constraints (44):
    c: Tangent(g0,g4) = -1.5708
    c: Tangent(g0,g5) = -1.5708
    c: Tangent(g1,g5) = -1.5708
    c: Tangent(g1,g6) = -1.5708
    c: Tangent(g2,g6) = -1.5708
    c: Tangent(g2,g7) = -1.5708
    c: Tangent(g3,g7) = -1.5708
    c: Tangent(g3,g4) = -1.5708
    c: Vertical(g0)
    c: Vertical(g2)
    c: Horizontal(g1)
    c: Equal(g4,g5)
    c: Equal(g5,g6)
    c: Equal(g6,g7)
    c: PointOnObject(g8,g0)
    c: PointOnObject(g8,g3)
    c: PointOnObject(g9,g1)
    c: PointOnObject(g9,g2)
    c: Coincident(g3,g-5)
    c: Equal(g-5,g7)
    c: Coincident(g3,g-3)
    c: Equal(g3,g2)
    c: Tangent(g10,g14) = -1.5708
    c: Tangent(g10,g15) = -1.5708
    c: Tangent(g11,g15) = -1.5708
    c: Tangent(g11,g16) = -1.5708
    c: Tangent(g12,g16) = -1.5708
    c: Tangent(g12,g17) = -1.5708
    c: Tangent(g13,g17) = -1.5708
    c: Tangent(g13,g14) = -1.5708
    c: Vertical(g10)
    c: Horizontal(g11)
    c: Equal(g14,g15)
    c: Equal(g15,g16)
    c: Equal(g16,g17)
    c: PointOnObject(g18,g10)
    c: PointOnObject(g18,g13)
    c: PointOnObject(g19,g11)
    c: PointOnObject(g19,g12)
    c: Symmetric(g12,g12,g-1)
    c: Symmetric(g13,g13,g-2)
    c: Equal(g11,g12)
    c: DistanceX(g12,g2) = 1
    c: Horizontal(g2,g12)
FEATURE [PartDesign::Pad] Pad007
  BaseFeature = -> LinearPattern003
  Direction = (0,0,1)
  Length = 3
  Length2 = 10
  Profile = -> Sketch009
  ReferenceAxis = -> Sketch009 [N_Axis]
  Refine = true
  Suppressed = false
  Type = 0
FEATURE [PartDesign::CoordinateSystem] FanHolder
  AttacherType = Attacher::AttachEngine3D
  AttachmentOffset = pos=(0,0,3) rot=(0,0,1;0rad)
  AttachmentSupport = -> [Pad007]
  MapMode = 11
  Placement = pos=(-35.75,35.75,4.5) rot=(0,0,1;1.5708rad)
FEATURE [PartDesign::Body] Body001  label="FilterHolder"
  AllowCompound = false
  Group = -> [Sketch006,Pad004,Sketch007,Pad005,LinearPattern002,Sketch008,Pad006,LinearPattern003,Sketch009,Pad007,FanHolder]
  Origin = -> Origin002
  Tip = -> Pad007
COMPONENT P2 — recipe-attached ("Base", modeled in this document).
Construction recipe (the document's own serialized feature program — sketch geometry with constraints, then the solid features built on it; lengths are millimeters unless a unit is written):

FEATURE [Sketcher::SketchObject] Sketch023
  ArcFitTolerance = 1e-06
  AttachmentSupport = -> [XY_Plane003]
  FullyConstrained = true
  MakeInternals = false
  MapMode = 5
  sketch-geometry (10):
    g0: LineSegment StartX=-55 StartY=25 StartZ=0 EndX=-55 EndY=-25 EndZ=0
    g1: LineSegment StartX=-45 StartY=-35 StartZ=0 EndX=45 EndY=-35 EndZ=0
    g2: LineSegment StartX=55 StartY=-25 StartZ=0 EndX=55 EndY=25 EndZ=0
    g3: LineSegment StartX=45 StartY=35 StartZ=0 EndX=-45 EndY=35 EndZ=0
    g4: ArcOfCircle CenterX=-45 CenterY=25 CenterZ=0 NormalX=0 NormalY=0 NormalZ=1 AngleXU=0 Radius=10 StartAngle=1.5708 EndAngle=3.14159
    g5: ArcOfCircle CenterX=-45 CenterY=-25 CenterZ=0 NormalX=0 NormalY=0 NormalZ=1 AngleXU=0 Radius=10 StartAngle=3.14159 EndAngle=4.71239
    g6: ArcOfCircle CenterX=45 CenterY=-25 CenterZ=0 NormalX=0 NormalY=0 NormalZ=1 AngleXU=0 Radius=10 StartAngle=4.71239 EndAngle=6.28319
    g7: ArcOfCircle CenterX=45 CenterY=25 CenterZ=0 NormalX=0 NormalY=0 NormalZ=1 AngleXU=0 Radius=10 StartAngle=1e-16 EndAngle=1.5708
    g8: GeomPoint [constr] X=-55 Y=35 Z=0
    g9: GeomPoint [constr] X=55 Y=-35 Z=0
  constraints (22):
    c: Tangent(g0,g4) = -1.5708
    c: Tangent(g0,g5) = -1.5708
    c: Tangent(g1,g5) = -1.5708
    c: Tangent(g1,g6) = -1.5708
    c: Tangent(g2,g6) = -1.5708
    c: Tangent(g2,g7) = -1.5708
    c: Tangent(g3,g7) = -1.5708
    c: Tangent(g3,g4) = -1.5708
    c: Vertical(g2)
    c: Horizontal(g1)
    c: Equal(g4,g5)
    c: Equal(g5,g6)
    c: Equal(g6,g7)
    c: PointOnObject(g8,g0)
    c: PointOnObject(g8,g3)
    c: PointOnObject(g9,g1)
    c: PointOnObject(g9,g2)
    c: Symmetric(g3,g3,g-2)
    c: Symmetric(g0,g0,g-1)
    c: DistanceX(g0,g2) = 110
    c: DistanceY(g1,g3) = 70
    c: Radius(g7) = 10
FEATURE [PartDesign::Pad] Pad014
  Direction = (0,0,1)
  Length = 20
  Length2 = 10
  Profile = -> Sketch023
  ReferenceAxis = -> Sketch023 [N_Axis]
  Refine = true
  Suppressed = false
  Type = 0
FEATURE [Sketcher::SketchObject] Sketch024
  ArcFitTolerance = 1e-06
  AttachmentSupport = -> [XZ_Plane003]
  ExternalGeometry = -> [Pad014]
  FullyConstrained = true
  MakeInternals = false
  MapMode = 5
  Placement = pos=(0,0,0) rot=(1,0,0;1.5708rad)
  sketch-geometry (5):
    g0: LineSegment StartX=55 StartY=20 StartZ=0 EndX=45 EndY=20 EndZ=0
    g1: ArcOfCircle CenterX=45 CenterY=16 CenterZ=0 NormalX=0 NormalY=0 NormalZ=1 AngleXU=0 Radius=4 StartAngle=0.413862 EndAngle=1.5708
    g2: ArcOfCircle CenterX=47 CenterY=1.5 CenterZ=0 NormalX=0 NormalY=0 NormalZ=1 AngleXU=0 Radius=8 StartAngle=3e-16 EndAngle=0.413862
    g3: LineSegment StartX=54.3246 StartY=4.71719 StartZ=0 EndX=48.6623 EndY=17.6086 EndZ=0
    g4: LineSegment StartX=55 StartY=20 StartZ=0 EndX=55 EndY=1.5 EndZ=0
  constraints (12):
    c: Horizontal(g0)
    c: Tangent(g1,g0) = -1.5708
    c: Tangent(g3,g2) = -1.5708
    c: Tangent(g3,g1) = -1.5708
    c: Coincident(g0,g-3)
    c: Coincident(g4,g0)
    c: PointOnObject(g4,g-3)
    c: Tangent(g4,g2) = 1.5708
    c: DistanceY(g2) = 1.5
    c: DistanceX(g0,g0) = 10
    c: Radius(g2) = 8
    c: Radius(g1) = 4
FEATURE [PartDesign::SubtractivePipe] SubtractivePipe
  AuxilleryCurvelinear = true
  AuxillerySpineTangent = false
  BaseFeature = -> Pad014
  Binormal = (0,0,0)
  Mode = 0
  Profile = -> Sketch024
  Refine = true
  Spine = -> Pad014 [Edge16,Edge19,Edge22,Edge24,Edge4,Edge7,Edge10,Edge13]
  SpineTangent = false
  Suppressed = false
  Transformation = 0
  Transition = 0
FEATURE [Sketcher::SketchObject] Sketch025
  ArcFitTolerance = 1e-06
  AttachmentSupport = -> [YZ_Plane003]
  ExternalGeometry = -> [SubtractivePipe]
  FullyConstrained = true
  MakeInternals = false
  MapMode = 5
  Placement = pos=(0,0,0) rot=(0.57735,0.57735,0.57735;2.0944rad)
  sketch-geometry (7):
    g0: LineSegment StartX=-7.5 StartY=20 StartZ=0 EndX=7.5 EndY=20 EndZ=0
    g1: ArcOfCircle CenterX=7.5 CenterY=23 CenterZ=0 NormalX=0 NormalY=0 NormalZ=1 AngleXU=0 Radius=3 StartAngle=3.14159 EndAngle=4.71239
    g2: ArcOfCircle CenterX=-7.5 CenterY=23 CenterZ=0 NormalX=0 NormalY=0 NormalZ=1 AngleXU=0 Radius=3 StartAngle=4.71239 EndAngle=6.28319
    g3: ArcOfCircle CenterX=8.84e-14 CenterY=28 CenterZ=0 NormalX=0 NormalY=0 NormalZ=1 AngleXU=0 Radius=4.5 StartAngle=-6.7475e-12 EndAngle=3.14159
    g4: LineSegment StartX=4.5 StartY=23 StartZ=0 EndX=4.5 EndY=28 EndZ=0
    g5: LineSegment StartX=-4.5 StartY=23 StartZ=0 EndX=-4.5 EndY=28 EndZ=0
    g6: Circle CenterX=8.84e-14 CenterY=28 CenterZ=0 NormalX=0 NormalY=0 NormalZ=1 AngleXU=0 Radius=2.75
  constraints (16):
    c: PointOnObject(g0,g-3)
    c: Symmetric(g0,g0,g-2)
    c: Vertical(g5)
    c: Tangent(g4,g3) = -1.5708
    c: Tangent(g4,g1) = 1.5708
    c: Tangent(g1,g0) = -1.5708
    c: Tangent(g2,g0) = -1.5708
    c: Tangent(g5,g2) = -1.5708
    c: Tangent(g5,g3) = 1.5708
    c: Vertical(g4)
    c: Equal(g1,g2)
    c: Diameter(g3) = 9
    c: Coincident(g6,g3)
    c: Diameter(g6) = 5.5
    c: Radius(g1) = 3
    c: DistanceY(g0,g3) = 8
FEATURE [PartDesign::Pad] Pad015
  BaseFeature = -> SubtractivePipe
  Direction = (1,0,0)
  Length = 70
  Length2 = 10
  Midplane = true
  Profile = -> Sketch025
  ReferenceAxis = -> Sketch025 [N_Axis]
  Refine = true
  Suppressed = false
  Type = 0
FEATURE [Sketcher::SketchObject] Sketch026
  ArcFitTolerance = 1e-06
  AttachmentSupport = -> [XZ_Plane003]
  ExternalGeometry = -> [Pad015]
  FullyConstrained = true
  MakeInternals = false
  MapMode = 5
  Placement = pos=(0,0,0) rot=(1,0,0;1.5708rad)
  sketch-geometry (5):
    g0: LineSegment StartX=-25.5 StartY=35 StartZ=0 EndX=-25.5 EndY=20 EndZ=0
    g1: LineSegment StartX=-25.5 StartY=20 StartZ=0 EndX=25.5 EndY=20 EndZ=0
    g2: LineSegment StartX=25.5 StartY=20 StartZ=0 EndX=25.5 EndY=35 EndZ=0
    g3: LineSegment StartX=25.5 StartY=35 StartZ=0 EndX=-25.5 EndY=35 EndZ=0
    g4: GeomPoint [constr] X=0 Y=27.5 Z=0
  constraints (13):
    c: Coincident(g0,g1)
    c: Coincident(g1,g2)
    c: Coincident(g2,g3)
    c: Coincident(g3,g0)
    c: Vertical(g0)
    c: Vertical(g2)
    c: Horizontal(g1)
    c: Horizontal(g3)
    c: Symmetric(g2,g0,g4)
    c: PointOnObject(g4,g-2)
    c: PointOnObject(g1,g-3)
    c: DistanceX(g3,g3) = 51
    c: DistanceY(g2,g2) = 15
FEATURE [PartDesign::Pocket] Pocket004
  BaseFeature = -> Pad015
  Direction = (0,1,-2e-16)
  Length = 5
  Length2 = 5
  Midplane = true
  Profile = -> Sketch026
  ReferenceAxis = -> Sketch026 [N_Axis]
  Refine = true
  Suppressed = false
  Type = 1
FEATURE [Sketcher::SketchObject] Sketch027
  ArcFitTolerance = 1e-06
  AttachmentSupport = -> [Pocket004]
  ExternalGeometry = -> [Pocket004]
  FullyConstrained = true
  MakeInternals = false
  MapMode = 5
  Placement = pos=(0,-30.5104,13.4011) rot=(1,0,0;1.15693rad)
  sketch-geometry (5):
    g0: LineSegment StartX=-34.25 StartY=0 StartZ=0 EndX=-34.25 EndY=-4 EndZ=0
    g1: LineSegment StartX=-34.25 StartY=-4 StartZ=0 EndX=-26.25 EndY=-4 EndZ=0
    g2: LineSegment StartX=-26.25 StartY=-4 StartZ=0 EndX=-26.25 EndY=0 EndZ=0
    g3: LineSegment StartX=-26.25 StartY=0 StartZ=0 EndX=-34.25 EndY=0 EndZ=0
    g4: LineSegment [constr] StartX=-30.25 StartY=0 StartZ=0 EndX=-30.25 EndY=15.2954 EndZ=0
  constraints (14):
    c: Coincident(g0,g1)
    c: Coincident(g1,g2)
    c: Coincident(g2,g3)
    c: Coincident(g3,g0)
    c: Vertical(g0)
    c: Vertical(g2)
    c: Horizontal(g1)
    c: Horizontal(g3)
    c: PointOnObject(g0,g-1)
    c: DistanceY(g2,g2) = 4
    c: DistanceX(g1,g1) = 8
    c: Symmetric(g3,g3,g4)
    c: Vertical(g4)
    c: Symmetric(g-3,g-3,g4)
FEATURE [PartDesign::Pocket] Pocket005
  BaseFeature = -> Pocket004
  Direction = (0,0.915575,-0.402148)
  Length = 10
  Length2 = 5
  Profile = -> Sketch027
  ReferenceAxis = -> Sketch027 [N_Axis]
  Refine = true
  Suppressed = false
  Type = 0
FEATURE [Sketcher::SketchObject] Sketch028
  ArcFitTolerance = 1e-06
  AttachmentSupport = -> [Pocket005]
  ExternalGeometry = -> [Pocket005]
  FullyConstrained = true
  MakeInternals = false
  MapMode = 5
  Placement = pos=(-2.8e-15,35,0) rot=(0,0.707107,0.707107;3.14159rad)
  sketch-geometry (6):
    g0: LineSegment StartX=24.25 StartY=15.1629 StartZ=0 EndX=24.25 EndY=7.16289 EndZ=0
    g1: LineSegment StartX=24.25 StartY=7.16289 StartZ=0 EndX=36.25 EndY=7.16289 EndZ=0
    g2: LineSegment StartX=36.25 StartY=7.16289 StartZ=0 EndX=36.25 EndY=15.1629 EndZ=0
    g3: LineSegment StartX=36.25 StartY=15.1629 StartZ=0 EndX=24.25 EndY=15.1629 EndZ=0
    g4: LineSegment [constr] StartX=30.25 StartY=15.1629 StartZ=0 EndX=30.25 EndY=23 EndZ=0
    g5: LineSegment [constr] StartX=45 StartY=11.1629 StartZ=0 EndX=36.25 EndY=11.1629 EndZ=0
  constraints (16):
    c: Coincident(g0,g1)
    c: Coincident(g1,g2)
    c: Coincident(g2,g3)
    c: Coincident(g3,g0)
    c: Vertical(g0)
    c: Vertical(g2)
    c: Horizontal(g1)
    c: Horizontal(g3)
    c: Symmetric(g3,g3,g4)
    c: Symmetric(g-3,g-3,g4)
    c: Vertical(g4)
    c: DistanceX(g3,g3) = 12
    c: DistanceY(g2,g2) = 8
    c: Symmetric(g-4,g-4,g5)
    c: Symmetric(g2,g2,g5)
    c: Horizontal(g5)
FEATURE [PartDesign::Pocket] Pocket006
  BaseFeature = -> Pocket005
  Direction = (0,-1,2e-16)
  Length = 63
  Length2 = 5
  Profile = -> Sketch028
  ReferenceAxis = -> Sketch028 [N_Axis]
  Refine = true
  Suppressed = false
  Type = 0
FEATURE [Sketcher::SketchObject] Sketch029
  ArcFitTolerance = 1e-06
  AttachmentSupport = -> [Pocket006]
  ExternalGeometry = -> [Pocket006]
  FullyConstrained = true
  MakeInternals = false
  MapMode = 5
  Placement = pos=(0,0,0) rot=(1,0,0;3.14159rad)
  sketch-geometry (10):
    g0: LineSegment StartX=-45 StartY=20 StartZ=0 EndX=-45 EndY=-20 EndZ=0
    g1: LineSegment StartX=-40 StartY=-25 StartZ=0 EndX=40 EndY=-25 EndZ=0
    g2: LineSegment StartX=45 StartY=-20 StartZ=0 EndX=45 EndY=20 EndZ=0
    g3: LineSegment StartX=40 StartY=25 StartZ=0 EndX=-40 EndY=25 EndZ=0
    g4: ArcOfCircle CenterX=-40 CenterY=20 CenterZ=0 NormalX=0 NormalY=0 NormalZ=1 AngleXU=0 Radius=5 StartAngle=1.5708 EndAngle=3.14159
    g5: ArcOfCircle CenterX=-40 CenterY=-20 CenterZ=0 NormalX=0 NormalY=0 NormalZ=1 AngleXU=0 Radius=5 StartAngle=3.14159 EndAngle=4.71239
    g6: ArcOfCircle CenterX=40 CenterY=-20 CenterZ=0 NormalX=0 NormalY=0 NormalZ=1 AngleXU=0 Radius=5 StartAngle=4.71239 EndAngle=6.28319
    g7: ArcOfCircle CenterX=40 CenterY=20 CenterZ=0 NormalX=0 NormalY=0 NormalZ=1 AngleXU=0 Radius=5 StartAngle=9.685e-13 EndAngle=1.5708
    g8: GeomPoint [constr] X=-45 Y=25 Z=0
    g9: GeomPoint [constr] X=45 Y=-25 Z=0
  constraints (22):
    c: Tangent(g0,g4) = -1.5708
    c: Tangent(g0,g5) = -1.5708
    c: Tangent(g1,g5) = -1.5708
    c: Tangent(g1,g6) = -1.5708
    c: Tangent(g2,g6) = -1.5708
    c: Tangent(g2,g7) = -1.5708
    c: Tangent(g3,g7) = -1.5708
    c: Tangent(g3,g4) = -1.5708
    c: Vertical(g2)
    c: Horizontal(g1)
    c: Equal(g4,g5)
    c: Equal(g5,g6)
    c: Equal(g6,g7)
    c: PointOnObject(g8,g0)
    c: PointOnObject(g8,g3)
    c: PointOnObject(g9,g1)
    c: PointOnObject(g9,g2)
    c: Radius(g5) = 5
    c: Symmetric(g3,g3,g-2)
    c: Symmetric(g0,g0,g-1)
    c: DistanceX(g2,g-3) = 10
    c: DistanceY(g3,g-4) = 10
FEATURE [PartDesign::Pocket] Pocket007
  BaseFeature = -> Pocket006
  Direction = (0,0,1)
  Length = 15
  Length2 = 5
  Profile = -> Sketch029
  ReferenceAxis = -> Sketch029 [N_Axis]
  Refine = true
  Suppressed = false
  Type = 0
FEATURE [PartDesign::CoordinateSystem] Fan  label="FanHolders"
  AttacherType = Attacher::AttachEngine3D
  AttachmentSupport = -> [Pocket007]
  MapMode = 45
  Placement = pos=(0,1.014e-13,28) rot=(0.57735,0.57735,0.57735;2.0944rad)
FEATURE [PartDesign::CoordinateSystem] Bottom
  AttacherType = Attacher::AttachEngine3D
  AttachmentSupport = -> [Pocket007]
  MapMode = 45
  Placement = pos=(-2.3879e-12,-1.227e-13,0) rot=(0,0,1;1.5708rad)
FEATURE [PartDesign::Body] Body002  label="Base"
  AllowCompound = false
  Group = -> [Sketch023,Pad014,Sketch024,SubtractivePipe,Sketch025,Pad015,Sketch026,Pocket004,Sketch027,Pocket005,Sketch028,Pocket006,Sketch029,Pocket007,Fan,Bottom]
  Origin = -> Origin003
  Tip = -> Pocket007
COMPONENT P3 — recipe-attached ("Fan2Holder", modeled in this document).
Construction recipe (the document's own serialized feature program — sketch geometry with constraints, then the solid features built on it; lengths are millimeters unless a unit is written):

FEATURE [Sketcher::SketchObject] Sketch014
  ArcFitTolerance = 1e-06
  AttachmentSupport = -> [XY_Plane004]
  FullyConstrained = true
  MakeInternals = false
  MapMode = 5
  sketch-geometry (13):
    g0: LineSegment StartX=-42.5 StartY=35.75 StartZ=0 EndX=-42.5 EndY=-35.75 EndZ=0
    g1: LineSegment StartX=-35.75 StartY=-42.5 StartZ=0 EndX=60 EndY=-42.5 EndZ=0
    g2: LineSegment StartX=60 StartY=-42.5 StartZ=0 EndX=60 EndY=42.5 EndZ=0
    g3: LineSegment StartX=60 StartY=42.5 StartZ=0 EndX=-35.75 EndY=42.5 EndZ=0
    g4: Circle CenterX=-35.75 CenterY=35.75 CenterZ=0 NormalX=0 NormalY=0 NormalZ=1 AngleXU=0 Radius=2.5
    g5: Circle CenterX=35.75 CenterY=35.75 CenterZ=0 NormalX=0 NormalY=0 NormalZ=1 AngleXU=0 Radius=2.5
    g6: Circle CenterX=-35.75 CenterY=-35.75 CenterZ=0 NormalX=0 NormalY=0 NormalZ=1 AngleXU=0 Radius=2.5
    g7: Circle CenterX=35.75 CenterY=-35.75 CenterZ=0 NormalX=0 NormalY=0 NormalZ=1 AngleXU=0 Radius=2.5
    g8: Circle CenterX=0 CenterY=0 CenterZ=0 NormalX=0 NormalY=0 NormalZ=1 AngleXU=0 Radius=38.75
    g9: ArcOfCircle CenterX=-35.75 CenterY=35.75 CenterZ=0 NormalX=0 NormalY=0 NormalZ=1 AngleXU=0 Radius=6.75 StartAngle=1.5708 EndAngle=3.14159
    g10: GeomPoint [constr] X=-42.5 Y=42.5 Z=0
    g11: ArcOfCircle CenterX=-35.75 CenterY=-35.75 CenterZ=0 NormalX=0 NormalY=0 NormalZ=1 AngleXU=0 Radius=6.75 StartAngle=3.14159 EndAngle=4.71239
    g12: GeomPoint [constr] X=-42.5 Y=-42.5 Z=0
  constraints (30):
    c: Coincident(g1,g2)
    c: Coincident(g2,g3)
    c: Vertical(g2)
    c: Horizontal(g1)
    c: Horizontal(g3)
    c: DistanceY(g12,g10) = 85
    c: Equal(g7,g5)
    c: Equal(g5,g4)
    c: Equal(g4,g6)
    c: Diameter(g7) = 5
    c: Symmetric(g7,g5,g-1)
    c: Symmetric(g5,g4,g-2)
    c: Vertical(g6,g4)
    c: Horizontal(g6,g7)
    c: DistanceX(g4,g5) = 71.5
    c: DistanceY(g6,g4) = 71.5
    c: Symmetric(g12,g10,g-1)
    c: Coincident(g8,g-1)
    c: Diameter(g8) = 77.5
    c: DistanceX(g10,g-1) = 42.5
    c: DistanceX(g1) = 60
    c: PointOnObject(g10,g0)
    c: PointOnObject(g10,g3)
    c: Tangent(g0,g9) = -1.5708
    c: Tangent(g3,g9) = -1.5708
    c: PointOnObject(g12,g1)
    c: Tangent(g0,g11) = -1.5708
    c: Tangent(g1,g11) = -1.5708
    c: Equal(g11,g9)
    c: Coincident(g9,g4)
FEATURE [PartDesign::Pad] Pad010
  Direction = (0,0,1)
  Length = 1.5
  Length2 = 10
  Profile = -> Sketch014
  ReferenceAxis = -> Sketch014 [N_Axis]
  Refine = true
  Suppressed = false
  Type = 0
FEATURE [Sketcher::SketchObject] Sketch015
  ArcFitTolerance = 1e-06
  AttachmentSupport = -> [Pad010]
  ExternalGeometry = -> [Pad010]
  FullyConstrained = true
  MakeInternals = false
  MapMode = 5
  Placement = pos=(0,0,1.5) rot=(0,0,1;0rad)
  sketch-geometry (12):
    g0: LineSegment StartX=60 StartY=42.5 StartZ=0 EndX=-35.75 EndY=42.5 EndZ=0
    g1: LineSegment StartX=-42.5 StartY=35.75 StartZ=0 EndX=-42.5 EndY=-35.75 EndZ=0
    g2: LineSegment StartX=-35.75 StartY=-42.5 StartZ=0 EndX=60 EndY=-42.5 EndZ=0
    g3: ArcOfCircle CenterX=-35.75 CenterY=-35.75 CenterZ=0 NormalX=0 NormalY=0 NormalZ=1 AngleXU=0 Radius=6.75 StartAngle=3.14159 EndAngle=4.71239
    g4: ArcOfCircle CenterX=-35.75 CenterY=35.75 CenterZ=0 NormalX=0 NormalY=0 NormalZ=1 AngleXU=0 Radius=6.75 StartAngle=1.5708 EndAngle=3.14159
    g5: LineSegment StartX=60 StartY=-42.5 StartZ=0 EndX=60 EndY=-41 EndZ=0
    g6: LineSegment StartX=60 StartY=-41 StartZ=0 EndX=-35.75 EndY=-41 EndZ=0
    g7: LineSegment StartX=-41 StartY=-35.75 StartZ=0 EndX=-41 EndY=35.75 EndZ=0
    g8: LineSegment StartX=-35.75 StartY=41 StartZ=0 EndX=60 EndY=41 EndZ=0
    g9: LineSegment StartX=60 StartY=41 StartZ=0 EndX=60 EndY=42.5 EndZ=0
    g10: ArcOfCircle CenterX=-35.75 CenterY=-35.75 CenterZ=0 NormalX=0 NormalY=0 NormalZ=1 AngleXU=0 Radius=5.25 StartAngle=3.14159 EndAngle=4.71239
    g11: ArcOfCircle CenterX=-35.75 CenterY=35.75 CenterZ=0 NormalX=0 NormalY=0 NormalZ=1 AngleXU=0 Radius=5.25 StartAngle=1.5708 EndAngle=3.14159
  constraints (30):
    c: Coincident(g0,g-3)
    c: Coincident(g0,g-4)
    c: Horizontal(g2)
    c: Symmetric(g2,g0,g-1)
    c: Equal(g2,g0)
    c: Coincident(g-5,g1)
    c: Coincident(g1,g-5)
    c: Coincident(g3,g2)
    c: Coincident(g3,g1)
    c: Coincident(g4,g1)
    c: Coincident(g4,g0)
    c: Equal(g4,g-4)
    c: Equal(g-4,g3)
    c: Coincident(g5,g2)
    c: Vertical(g5)
    c: Coincident(g6,g5)
    c: Horizontal(g6)
    c: Vertical(g7)
    c: Coincident(g9,g8)
    c: Coincident(g9,g0)
    c: Horizontal(g8)
    c: Vertical(g9)
    c: Equal(g5,g9)
    c: Equal(g6,g8)
    c: Tangent(g10,g6) = 1.5708
    c: Tangent(g10,g7) = 1.5708
    c: Tangent(g11,g7) = 1.5708
    c: Tangent(g11,g8) = 1.5708
    c: DistanceY(g5,g5) = 1.5
    c: Coincident(g11,g4)
FEATURE [PartDesign::Pad] Pad011
  BaseFeature = -> Pad010
  Direction = (0,0,1)
  Length = 5
  Length2 = 10
  Profile = -> Sketch015
  ReferenceAxis = -> Sketch015 [N_Axis]
  Refine = true
  Suppressed = false
  Type = 0
FEATURE [Sketcher::SketchObject] Sketch016
  ArcFitTolerance = 1e-06
  AttachmentSupport = -> [Pad011]
  ExternalGeometry = -> [Pad011]
  FullyConstrained = true
  MakeInternals = false
  MapMode = 5
  Placement = pos=(60,0,0) rot=(0.57735,0.57735,0.57735;2.0944rad)
  sketch-geometry (6):
    g0: LineSegment StartX=41.1112 StartY=6.9583 StartZ=0 EndX=45 EndY=14.5 EndZ=0
    g1: LineSegment StartX=45 StartY=14.5 StartZ=0 EndX=46.5 EndY=14.5 EndZ=0
    g2: LineSegment StartX=46.5 StartY=14.5 StartZ=0 EndX=42.6112 EndY=6.9583 EndZ=0
    g3: ArcOfCircle CenterX=43.5 CenterY=6.5 CenterZ=0 NormalX=0 NormalY=0 NormalZ=1 AngleXU=0 Radius=1 StartAngle=2.66551 EndAngle=3.14159
    g4: ArcOfCircle CenterX=42 CenterY=6.5 CenterZ=0 NormalX=0 NormalY=0 NormalZ=1 AngleXU=0 Radius=1 StartAngle=2.66551 EndAngle=3.14159
    g5: LineSegment StartX=42.5 StartY=6.5 StartZ=0 EndX=41 EndY=6.5 EndZ=0
  constraints (16):
    c: Coincident(g0,g1)
    c: Horizontal(g1)
    c: Coincident(g1,g2)
    c: Coincident(g3,g-3)
    c: Coincident(g4,g-3)
    c: Tangent(g4,g0) = 1.5708
    c: Tangent(g3,g2) = -1.5708
    c: Coincident(g5,g3)
    c: Coincident(g5,g4)
    c: Perpendicular(g3,g5)
    c: Perpendicular(g4,g5)
    c: Equal(g1,g5)
    c: Radius(g4) = 1
    c: DistanceY(g3,g1) = 8
    c: DistanceX(g3,g1) = 4
    c: Equal(g4,g3)
FEATURE [PartDesign::AdditivePipe] AdditivePipe001
  AuxilleryCurvelinear = true
  AuxillerySpineTangent = false
  BaseFeature = -> Pad011
  Binormal = (0,0,0)
  Mode = 0
  Profile = -> Sketch016
  Refine = true
  Spine = -> Pad011 [Edge32,Edge33,Edge34,Edge35,Edge36]
  SpineTangent = false
  Suppressed = false
  Transformation = 0
  Transition = 0
FEATURE [Sketcher::SketchObject] Sketch017
  ArcFitTolerance = 1e-06
  AttachmentSupport = -> [XY_Plane004]
  ExternalGeometry = -> [AdditivePipe001]
  FullyConstrained = true
  MakeInternals = false
  MapMode = 5
  sketch-geometry (5):
    g0: LineSegment StartX=-30.75 StartY=42.5 StartZ=0 EndX=-30.75 EndY=-42.5 EndZ=0
    g1: LineSegment StartX=-30.75 StartY=-42.5 StartZ=0 EndX=-29.25 EndY=-42.5 EndZ=0
    g2: LineSegment StartX=-29.25 StartY=-42.5 StartZ=0 EndX=-29.25 EndY=42.5 EndZ=0
    g3: LineSegment StartX=-29.25 StartY=42.5 StartZ=0 EndX=-30.75 EndY=42.5 EndZ=0
    g4: GeomPoint [constr] X=-30 Y=0 Z=0
  constraints (13):
    c: Coincident(g0,g1)
    c: Coincident(g1,g2)
    c: Coincident(g2,g3)
    c: Coincident(g3,g0)
    c: Vertical(g0)
    c: Vertical(g2)
    c: Horizontal(g1)
    c: Horizontal(g3)
    c: Symmetric(g2,g0,g4)
    c: PointOnObject(g4,g-1)
    c: PointOnObject(g1,g-3)
    c: DistanceX(g3,g3) = 1.5
    c: DistanceX(g4,g-1) = 30
FEATURE [PartDesign::Pad] Pad012
  BaseFeature = -> AdditivePipe001
  Direction = (0,0,1)
  Length = 10
  Length2 = 10
  Profile = -> Sketch017
  ReferenceAxis = -> Sketch017 [N_Axis]
  Refine = true
  Suppressed = false
  Type = 3
  UpToFace = -> AdditivePipe001 [Face2]
FEATURE [PartDesign::LinearPattern] LinearPattern004
  BaseFeature = -> Pad012
  Direction = -> Sketch017 [H_Axis]
  Length = 60
  Mode = 0
  Occurrences = 5
  Offset = 15
  Originals = -> [Pad012]
  Refine = true
  Suppressed = false
  TransformMode = 0
FEATURE [Sketcher::SketchObject] Sketch018
  ArcFitTolerance = 1e-06
  AttachmentSupport = -> [XY_Plane004]
  ExternalGeometry = -> [LinearPattern004]
  FullyConstrained = true
  MakeInternals = false
  MapMode = 5
  sketch-geometry (5):
    g0: LineSegment StartX=42.5 StartY=29.25 StartZ=0 EndX=42.5 EndY=30.75 EndZ=0
    g1: LineSegment StartX=42.5 StartY=30.75 StartZ=0 EndX=-42.5 EndY=30.75 EndZ=0
    g2: LineSegment StartX=-42.5 StartY=30.75 StartZ=0 EndX=-42.5 EndY=29.25 EndZ=0
    g3: LineSegment StartX=-42.5 StartY=29.25 StartZ=0 EndX=42.5 EndY=29.25 EndZ=0
    g4: GeomPoint [constr] X=0 Y=30 Z=0
  constraints (13):
    c: Coincident(g0,g1)
    c: Coincident(g1,g2)
    c: Coincident(g2,g3)
    c: Coincident(g3,g0)
    c: Vertical(g0)
    c: Vertical(g2)
    c: Horizontal(g1)
    c: Horizontal(g3)
    c: Symmetric(g2,g0,g4)
    c: PointOnObject(g4,g-2)
    c: PointOnObject(g1,g-3)
    c: DistanceY(g4) = 30
    c: DistanceY(g0,g0) = 1.5
FEATURE [PartDesign::Pad] Pad013
  BaseFeature = -> LinearPattern004
  Direction = (0,0,1)
  Length = 10
  Length2 = 10
  Profile = -> Sketch018
  ReferenceAxis = -> Sketch018 [N_Axis]
  Refine = true
  Suppressed = false
  Type = 3
  UpToFace = -> LinearPattern004 [Face31]
FEATURE [PartDesign::LinearPattern] LinearPattern005
  BaseFeature = -> Pad013
  Direction = -> Sketch018 [V_Axis]
  Length = 60
  Mode = 0
  Occurrences = 5
  Offset = 15
  Originals = -> [Pad013]
  Refine = true
  Reversed = true
  Suppressed = false
  TransformMode = 0
FEATURE [PartDesign::CoordinateSystem] FanMountHole001
  AttacherType = Attacher::AttachEngine3D
  AttachmentSupport = -> [LinearPattern005]
  MapMode = 11
  Placement = pos=(-35.75,-35.75,0) rot=(0,0,1;1.5708rad)
FEATURE [Sketcher::SketchObject] Sketch019
  ArcFitTolerance = 1e-06
  AttachmentSupport = -> [XZ_Plane004]
  ExternalGeometry = -> [LinearPattern005]
  FullyConstrained = true
  MakeInternals = false
  MapMode = 5
  Placement = pos=(0,0,0) rot=(1,0,0;1.5708rad)
  sketch-geometry (4):
    g0: LineSegment StartX=60 StartY=14.5 StartZ=0 EndX=60 EndY=0 EndZ=0
    g1: LineSegment StartX=60 StartY=0 StartZ=0 EndX=43 EndY=0 EndZ=0
    g2: LineSegment StartX=43 StartY=0 StartZ=0 EndX=40.4433 EndY=14.5 EndZ=0
    g3: LineSegment StartX=40.4433 StartY=14.5 StartZ=0 EndX=60 EndY=14.5 EndZ=0
  constraints (11):
    c: Coincident(g-3,g0)
    c: PointOnObject(g0,g-1)
    c: Vertical(g0)
    c: Coincident(g0,g1)
    c: PointOnObject(g1,g-1)
    c: Coincident(g1,g2)
    c: PointOnObject(g2,g-3)
    c: Coincident(g2,g3)
    c: Coincident(g3,g0)
    c: DistanceX(g-1,g1) = 43
    c: Angle(g1,g2) = 1.74533
FEATURE [PartDesign::Pocket] Pocket002
  BaseFeature = -> LinearPattern005
  Direction = (0,1,-2e-16)
  Length = 5
  Length2 = 5
  Midplane = true
  Profile = -> Sketch019
  ReferenceAxis = -> Sketch019 [N_Axis]
  Refine = true
  Suppressed = false
  Type = 1
FEATURE [PartDesign::CoordinateSystem] FilterHolderMount001
  AttacherType = Attacher::AttachEngine3D
  AttachmentSupport = -> [Pocket002]
  MapMode = 11
  Placement = pos=(-35.75,35.75,1.5) rot=(0,0,1;1.5708rad)
FEATURE [PartDesign::CoordinateSystem] OtherFanHolder001
  AttacherType = Attacher::AttachEngine3D
  AttachmentSupport = -> [Pocket002]
  MapMode = 45
  Placement = pos=(42.8701,0,0.736527) rot=(0.642788,0,0.766044;3.14159rad)
FEATURE [Sketcher::SketchObject] Sketch022
  ArcFitTolerance = 1e-06
  FullyConstrained = true
  MakeInternals = false
  MapMode = 5
  Placement = pos=(41.7034,1.6e-15,7.35343) rot=(0.540716,0.540716,0.6444;1.99673rad)
  sketch-geometry (6):
    g0: ArcOfCircle CenterX=43.0908 CenterY=-0.761797 CenterZ=0 NormalX=0 NormalY=0 NormalZ=1 AngleXU=0 Radius=0.6 StartAngle=2.49691 EndAngle=3.31716
    g1: LineSegment StartX=44.66 StartY=3.6334 StartZ=0 EndX=42.6112 EndY=-0.401229 EndZ=0
    g2: LineSegment StartX=42.5 StartY=-5.3666 StartZ=0 EndX=42.5 EndY=-0.866599 EndZ=0
    g3: LineSegment StartX=42.5 StartY=-5.3666 StartZ=0 EndX=50.5 EndY=-5.3666 EndZ=0
    g4: LineSegment StartX=44.66 StartY=3.6334 StartZ=0 EndX=50.5 EndY=3.6334 EndZ=0
    g5: ArcOfCircle CenterX=50.5 CenterY=-0.866599 CenterZ=0 NormalX=0 NormalY=0 NormalZ=1 AngleXU=0 Radius=4.5 StartAngle=4.71239 EndAngle=7.85398
  constraints (16):
    c: Coincident(g0,g-3)
    c: Coincident(g0,g-4)
    c: Radius(g0) = 0.6
    c: Coincident(g3,g2)
    c: Horizontal(g3)
    c: Coincident(g4,g1)
    c: Horizontal(g4)
    c: Diameter(g5) = 9
    c: PointOnObject(g1,g-4)
    c: Horizontal(g5,g2)
    c: Tangent(g5,g3) = -1.5708
    c: Tangent(g5,g4) = 1.5708
    c: DistanceX(g-4,g5) = 4
    c: Coincident(g2,g0)
    c: Coincident(g0,g1)
    c: PointOnObject(g2,g-3)
FEATURE [PartDesign::Pocket] Pocket003
  BaseFeature = -> Pocket002
  Direction = (-0.984808,2e-16,-0.173648)
  Length = 50
  Length2 = 5
  Midplane = true
  Profile = -> Sketch022
  ReferenceAxis = -> Sketch022 [N_Axis]
  Refine = true
  Suppressed = false
  Type = 0
FEATURE [PartDesign::Body] Body003  label="Fan2Holder"
  AllowCompound = false
  Group = -> [Sketch014,Pad010,Sketch015,Pad011,Sketch016,AdditivePipe001,Sketch017,Pad012,LinearPattern004,Sketch018,Pad013,LinearPattern005,FanMountHole001,Sketch019,Pocket002,OtherFanHolder001,FilterHolderMount001,Sketch022,Pocket003]
  Origin = -> Origin004
  Tip = -> Pocket003
COMPONENT P4 — recipe-attached ("BottomCover", modeled in this document).
Construction recipe (the document's own serialized feature program — sketch geometry with constraints, then the solid features built on it; lengths are millimeters unless a unit is written):

FEATURE [Sketcher::SketchObject] Sketch030
  ArcFitTolerance = 1e-06
  AttachmentSupport = -> [XY_Plane005]
  FullyConstrained = true
  MakeInternals = false
  MapMode = 5
  sketch-geometry (10):
    g0: LineSegment StartX=-55 StartY=25 StartZ=0 EndX=-55 EndY=-25 EndZ=0
    g1: LineSegment StartX=-45 StartY=-35 StartZ=0 EndX=45 EndY=-35 EndZ=0
    g2: LineSegment StartX=55 StartY=-25 StartZ=0 EndX=55 EndY=25 EndZ=0
    g3: LineSegment StartX=45 StartY=35 StartZ=0 EndX=-45 EndY=35 EndZ=0
    g4: ArcOfCircle CenterX=-45 CenterY=25 CenterZ=0 NormalX=0 NormalY=0 NormalZ=1 AngleXU=0 Radius=10 StartAngle=1.5708 EndAngle=3.14159
    g5: ArcOfCircle CenterX=-45 CenterY=-25 CenterZ=0 NormalX=0 NormalY=0 NormalZ=1 AngleXU=0 Radius=10 StartAngle=3.14159 EndAngle=4.71239
    g6: ArcOfCircle CenterX=45 CenterY=-25 CenterZ=0 NormalX=0 NormalY=0 NormalZ=1 AngleXU=0 Radius=10 StartAngle=4.71239 EndAngle=6.28319
    g7: ArcOfCircle CenterX=45 CenterY=25 CenterZ=0 NormalX=0 NormalY=0 NormalZ=1 AngleXU=0 Radius=10 StartAngle=0 EndAngle=1.5708
    g8: GeomPoint [constr] X=-55 Y=35 Z=0
    g9: GeomPoint [constr] X=55 Y=-35 Z=0
  constraints (22):
    c: Tangent(g0,g4) = -1.5708
    c: Tangent(g0,g5) = -1.5708
    c: Tangent(g1,g5) = -1.5708
    c: Tangent(g1,g6) = -1.5708
    c: Tangent(g2,g6) = -1.5708
    c: Tangent(g2,g7) = -1.5708
    c: Tangent(g3,g7) = -1.5708
    c: Tangent(g3,g4) = -1.5708
    c: Vertical(g2)
    c: Horizontal(g1)
    c: Equal(g4,g5)
    c: Equal(g5,g6)
    c: Equal(g6,g7)
    c: PointOnObject(g8,g0)
    c: PointOnObject(g8,g3)
    c: PointOnObject(g9,g1)
    c: PointOnObject(g9,g2)
    c: Radius(g5) = 10
    c: Symmetric(g3,g3,g-2)
    c: Symmetric(g0,g0,g-1)
    c: DistanceX(g0,g2) = 110
    c: DistanceY(g1,g3) = 70
FEATURE [PartDesign::Pad] Pad016
  Direction = (0,0,1)
  Length = 1.5
  Length2 = 10
  Profile = -> Sketch030
  ReferenceAxis = -> Sketch030 [N_Axis]
  Refine = true
  Suppressed = false
  Type = 0
FEATURE [PartDesign::CoordinateSystem] Base001  label="Base002"
  AttacherType = Attacher::AttachEngine3D
  AttachmentSupport = -> [Pad016]
  MapMode = 45
  Placement = pos=(-8.91e-14,-6.93e-14,1.5) rot=(0,0,1;1.5708rad)
FEATURE [PartDesign::Body] Body004  label="BottomCover"
  AllowCompound = false
  Group = -> [Sketch030,Base001,Pad016]
  Origin = -> Origin005
  Tip = -> Pad016
PROVENANCE & LICENSES
A FreeCAD (.FCStd) document from a public repository crawl; recipes are the document's own serialized feature recipes (and, for linked parts, companion documents' recipes).
License: as declared in the source repository (recorded in the dataset sidecar).
